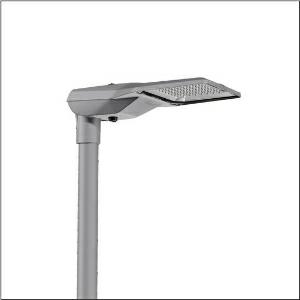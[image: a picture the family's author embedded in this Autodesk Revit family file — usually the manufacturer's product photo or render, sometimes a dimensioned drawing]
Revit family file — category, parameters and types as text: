
# Revit family: streetlight_sl_21_iq_midi___p0_5a_5xe3v31y08mb_e986
name_source: partatom
category: Lighting Fixtures
units: mm (PartAtom-declared; Revit-internal decimal feet)

## family parameters
Cut with Voids When Loaded = No
Host = Face
Light Source = No
Part Type = Normal
Room Calculation Point = No
Round Connector Dimension = Use Diameter
Shared = No

## types (1)
- --- (1 x LED, 18020 lm, 129.3 W, 3000K)
    Apparent Load = 129 VA
    CIE Flux Codes = 37 73 96 100 100
    Color Rendering = 70
    Color Temperature = 3000K
    Default Elevation = 1800 mm
    Description = Streetlight SL 21 iQ midi, mast luminaire, primary light control with lens, of PMMA, primary optical cover: cover, of toughened safety glass, transparent, light distribution: P0.5a, light emission: direct distribution, primary light characteristic: asymmetric, installation type: post-top, side-entry, LED, High Power LED, rated luminous flux: 18.020lm, luminous efficacy: 139lm/W, light colour: 730, colour temperature: 3000K, control gear: iQ-Street Remote, D4i with power reduction, control: pre-setting: logarithmic dimming characteristic, Street-Remote, Auto-Match, Temp-Guard, Lumen-Switch, Night-Set, Smart-Wire, Light-Fading, Desk-Remote (wireless, voltage-free reading and setting of iQ features in the workshop via application-optimized NFC function/RFID function), optimised constant luminous flux control (CLO 2.0), mains connection: 230..240V, AC, 50/60Hz, start of lifetime: 129W, end of service life: 142W, reduction: 56W, luminaire housing, of diecast aluminium, powder-coated, Siteco® metallic grey (DB 702S), corrosivity category C5 mid according to DIN EN ISO 12944, please order mast flange separately, inclination adjustable: 0°, 5°, 10°, 15°, sealing non-destructively replaceable, multi-level sealing system, length: 644mm, width: 335mm, height: 110mm, mast flange for spigot size: 42mm (side-entry): 5XC10008XM4, 60/48mm (side-entry/post-top): 5XC10108XM2, 76/60mm (side-entry/post-top): 5XC10108XM1, mounting height: 4..8m, Smart Interface below and above, protection rating (complete): IP66, insulation class (complete): insulation class II (safety insulation), certification: CE, ENEC, ENEC+, VDE, impact resistance: IK10, permissible operating ambient temperature for outdoor applications: -40..+50°C, standard-compliant lighting for roads and squares, packaging unit: 1 piece

Light Distribution: P0.5a
    Height = 111 mm
    Lamp = 1 x LED
    Lamp Light Flux = 18020 lm
    Lamp Power = 129.3 W
    Lamp count = 1
    Length = 644 mm
    Luminous efficacy = 139 lm/W
    Manufacturer = Siteco
    ModVariant = No
    Model = 5XE3V31Y08MB
    Number of Poles = 1
    OnlyDefault = Yes
    Power Factor = 1
    Product Name = Streetlight SL 21 iQ midi | P0.5a
    Product group = mast luminaire | pylon top
    ProductGroupID = 6100
    Protection Class = Protection class II
    Protection Degree = IP 66
    RLX_Detail_Level = 1
    RLX_Emergency_Light_Flux = 0 lm
    RLX_Emergency_Type = 0
    RLX_Emergency_Type_DB = No
    RlxData = <blob elided: 91761 chars, md5=ca2e4e0b>
    Socket = socket
    Standby Power = 0 W
    System Light Flux = 18021 lm
    System Power = 129 W
    Type Comments = factory setting: luminous flux: 100 % | dim-lin: 254 | 672 mA
    Type Image = l_1004304.jpg
    URL = http://relux.com
    VarID = @adj_091965
    Voltage = 0 V
    Weight = 0.00 kg
    Width = 336 mm

## geometry (parser evidence)
native form markers: Blend x4, Sweep x14
no freeform markers — native parametric forms only
